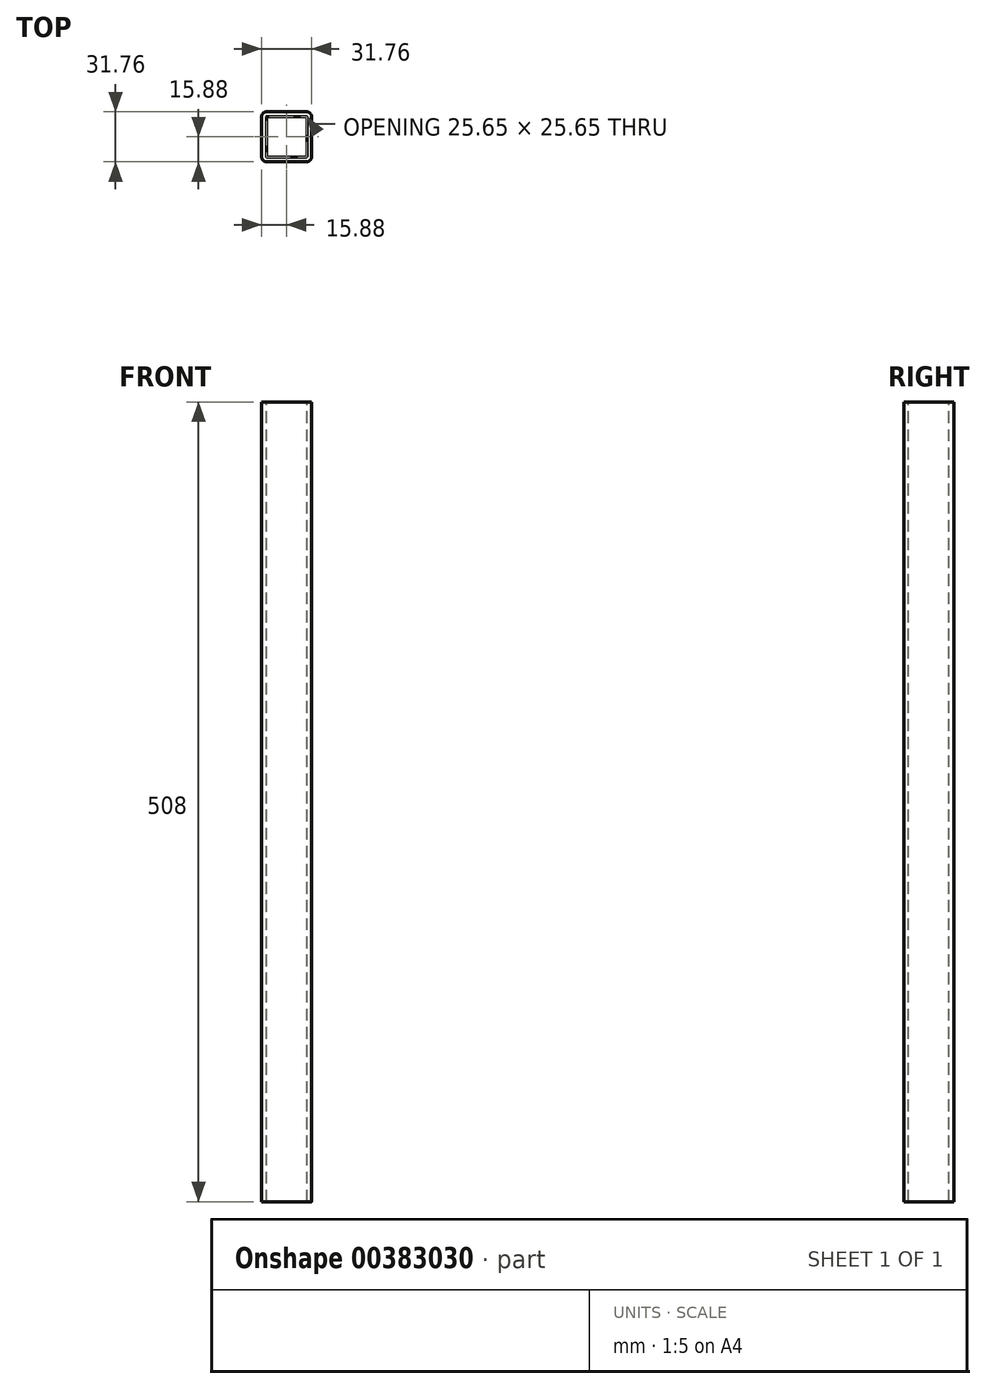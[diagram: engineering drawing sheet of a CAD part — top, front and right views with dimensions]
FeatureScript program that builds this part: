
annotation { "Feature Type Name" : "Feature", "Feature Type Description" : "" }
export const myFeature = defineFeature(function(context is Context, id is Id, definition is map)
    precondition{}
    {
        {
            var Q0;
            Q0=qCreatedBy(makeId("Top.planeOp"),FACE);
            var sketch = newSketch(context, id + "F0", { "sketchPlane" : qUnion([Q0])});
            skLineSegment(sketch, "E0.bottom", {"start": v(15.88, 15.88) * mm, "end": v(-15.88, 15.88) * mm});
            skLineSegment(sketch, "E0.top", {"start": v(15.88, -15.88) * mm, "end": v(-15.88, -15.88) * mm});
            skLineSegment(sketch, "E0.left", {"start": v(15.88, 15.88) * mm, "end": v(15.88, -15.88) * mm});
            skLineSegment(sketch, "E0.right", {"start": v(-15.88, 15.88) * mm, "end": v(-15.88, -15.88) * mm});
            skPoint(sketch, "E0.middle", {"position": v(0, 0) * mm});
            skSolve(sketch);
        }
        {
            var Q0;
            Q0=qSketchRegion(id+"F0",true);
            extrude(context, id + "F1", {"entities" : qUnion([Q0]), "oppositeDirection" : true, "depth" : 508 * mm});
        }
        {
            var Q0;
            Q0=makeQuery(id+"F1.opExtrude","SWEPT_EDGE",EDGE,{"disambiguationData":[OSD([sQuery(id+"F0.wireOp",EDGE,"E0.bottom"),sQuery(id+"F0.wireOp",EDGE,"E0.right")])]});
            var Q1;
            Q1=makeQuery(id+"F1.opExtrude","SWEPT_EDGE",EDGE,{"disambiguationData":[OSD([sQuery(id+"F0.wireOp",EDGE,"E0.top"),sQuery(id+"F0.wireOp",EDGE,"E0.right")])]});
            var Q2;
            Q2=makeQuery(id+"F1.opExtrude","SWEPT_EDGE",EDGE,{"disambiguationData":[OSD([sQuery(id+"F0.wireOp",EDGE,"E0.bottom"),sQuery(id+"F0.wireOp",EDGE,"E0.left")])]});
            var Q3;
            Q3=makeQuery(id+"F1.opExtrude","SWEPT_EDGE",EDGE,{"disambiguationData":[OSD([sQuery(id+"F0.wireOp",EDGE,"E0.top"),sQuery(id+"F0.wireOp",EDGE,"E0.left")])]});
            fillet(context, id + "F2", {"entities" : qUnion([Q0, Q1, Q2, Q3]), "radius" : 3.17 * mm, "tangentPropagation" : true, "allowEdgeOverflow" : false});
        }
        {
            var Q0;
            Q0=makeQuery(id+"F1.opExtrude","CAP_FACE",FACE,{"disambiguationData":[OSD([sQuery(id+"F0.wireOp",EDGE,"E0.bottom"),sQuery(id+"F0.wireOp",EDGE,"E0.top"),sQuery(id+"F0.wireOp",EDGE,"E0.left"),sQuery(id+"F0.wireOp",EDGE,"E0.right")])],"isStart":true});
            var Q1;
            Q1=makeQuery(id+"F1.opExtrude","CAP_FACE",FACE,{"disambiguationData":[OSD([sQuery(id+"F0.wireOp",EDGE,"E0.bottom"),sQuery(id+"F0.wireOp",EDGE,"E0.top"),sQuery(id+"F0.wireOp",EDGE,"E0.left"),sQuery(id+"F0.wireOp",EDGE,"E0.right")])],"isStart":false});
            shell(context, id + "F3", {"entities" : qUnion([Q0, Q1]), "thickness" : 3.05 * mm});
        }
    });
